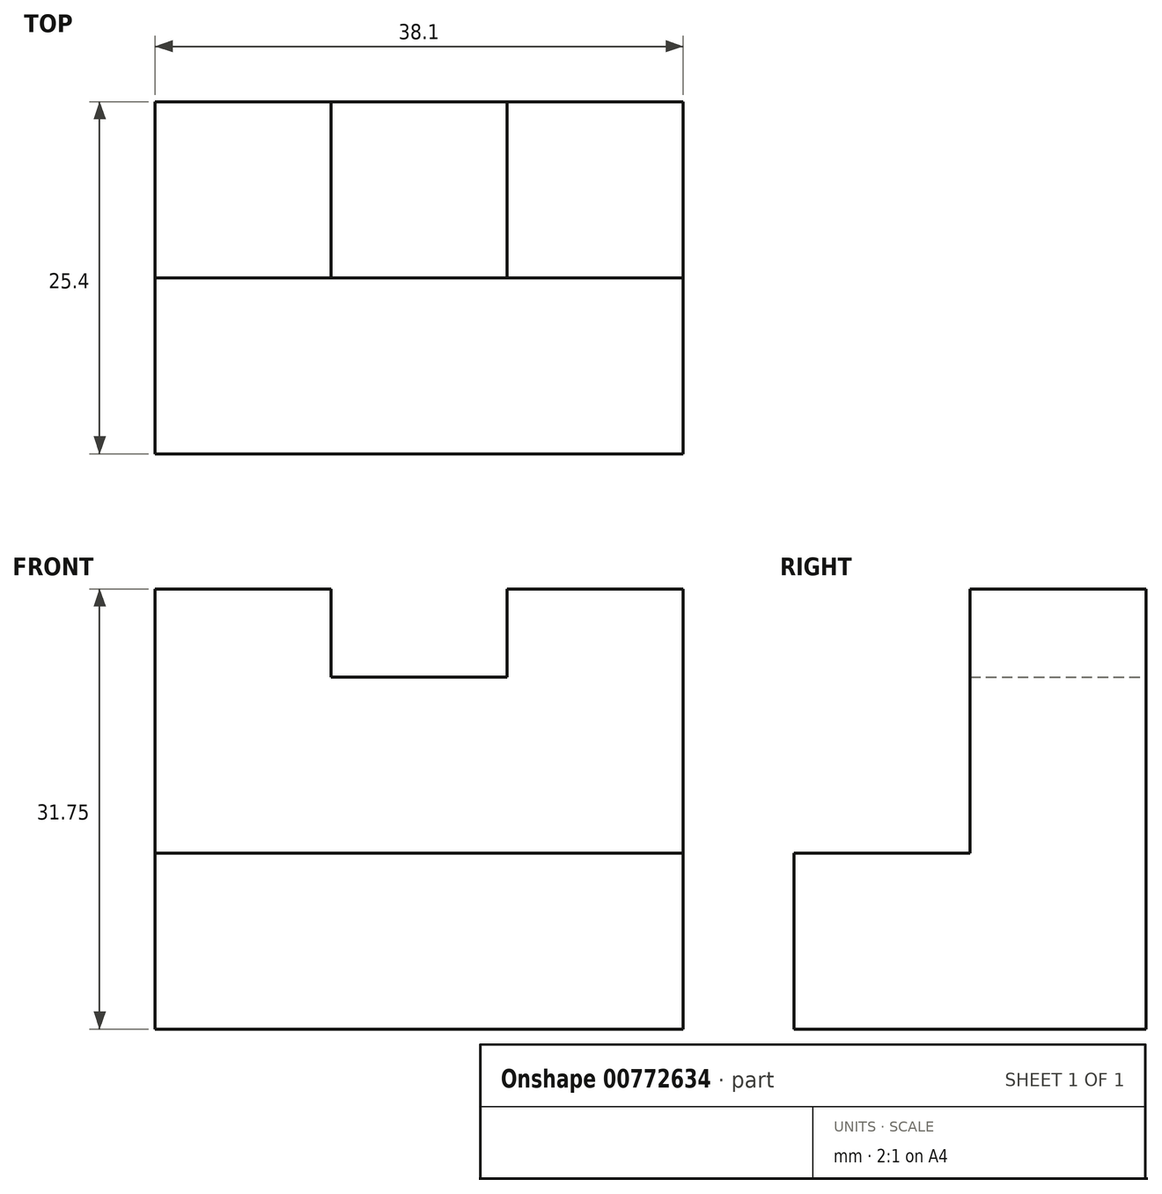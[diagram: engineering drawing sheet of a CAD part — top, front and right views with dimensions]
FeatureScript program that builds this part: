
annotation { "Feature Type Name" : "Feature", "Feature Type Description" : "" }
export const myFeature = defineFeature(function(context is Context, id is Id, definition is map)
    precondition{}
    {
        {
            var Q0;
            Q0=qCreatedBy(makeId("Front.planeOp"),FACE);
            var sketch = newSketch(context, id + "F0", { "sketchPlane" : qUnion([Q0])});
            skLineSegment(sketch, "E0", {"start": v(0, 0) * mm, "end": v(38.1, 0) * mm});
            skLineSegment(sketch, "E1", {"start": v(38.1, 0) * mm, "end": v(38.1, 31.75) * mm});
            skLineSegment(sketch, "E2", {"start": v(38.1, 31.75) * mm, "end": v(0, 31.75) * mm});
            skLineSegment(sketch, "E3", {"start": v(0, 31.75) * mm, "end": v(0, 0) * mm});
            skSolve(sketch);
        }
        {
            var Q0;
            Q0 = qSketchRegion(id + "F0", true);
            extrude(context, id + "F1", {"entities" : qUnion([Q0]), "depth" : 25.4 * mm, "offsetDistance" : 25.4 * mm});
        }
        {
            var Q0;
            Q0=makeQuery(id+"F1.opExtrude","SWEPT_FACE",FACE,{"disambiguationData":[OSD([sQuery(id+"F0.wireOp",EDGE,"E1")])]});
            var sketch = newSketch(context, id + "F2", { "sketchPlane" : qUnion([Q0])});
            skLineSegment(sketch, "E4", {"start": v(-25.4, 0) * mm, "end": v(-25.4, 12.7) * mm});
            skLineSegment(sketch, "E5", {"start": v(-25.4, 12.7) * mm, "end": v(-12.7, 12.7) * mm});
            skLineSegment(sketch, "E6", {"start": v(-12.7, 12.7) * mm, "end": v(-12.7, 31.75) * mm});
            skSolve(sketch);
        }
        {
            var Q0;
            {var subQ0=sQuery(id+"F2.wireOp",EDGE,"E5");Q0=makeQuery(id+"F2.imprint","IMPRINT",FACE,{"disambiguationData":[TD([[makeQuery(id+"F2.imprint","IMPRINT",EDGE,{"derivedFrom":subQ0}),1.0]])]});}
            extrude(context, id + "F3", {"entities" : qUnion([Q0]), "operationType" : NewBodyOperationType.REMOVE, "oppositeDirection" : true, "depth" : 38.1 * mm, "offsetDistance" : 25.4 * mm});
        }
        {
            var Q0;
            Q0=makeQuery(id+"F1.opExtrude","SWEPT_FACE",FACE,{"disambiguationData":[OSD([sQuery(id+"F0.wireOp",EDGE,"E2")])]});
            var sketch = newSketch(context, id + "F4", { "sketchPlane" : qUnion([Q0])});
            skLineSegment(sketch, "E7", {"start": v(38.1, -12.7) * mm, "end": v(25.4, -12.7) * mm});
            skLineSegment(sketch, "E8", {"start": v(25.4, -12.7) * mm, "end": v(25.4, 0) * mm});
            skLineSegment(sketch, "E9", {"start": v(25.4, 0) * mm, "end": v(38.1, 0) * mm});
            skLineSegment(sketch, "E10", {"start": v(38.1, 0) * mm, "end": v(38.1, -12.7) * mm});
            skLineSegment(sketch, "E11", {"start": v(25.4, -12.7) * mm, "end": v(12.7, -12.7) * mm});
            skLineSegment(sketch, "E12", {"start": v(12.7, -12.7) * mm, "end": v(12.7, 0) * mm});
            skLineSegment(sketch, "E13", {"start": v(12.7, 0) * mm, "end": v(25.4, 0) * mm});
            skLineSegment(sketch, "E14", {"start": v(12.7, 0) * mm, "end": v(0, 0) * mm});
            skLineSegment(sketch, "E15", {"start": v(0, 0) * mm, "end": v(0, -12.7) * mm});
            skLineSegment(sketch, "E16", {"start": v(0, -12.7) * mm, "end": v(12.7, -12.7) * mm});
            skSolve(sketch);
        }
        {
            var Q0;
            Q0=makeQuery(id+"F4.imprint","IMPRINT",FACE,{"disambiguationData":[TD([[makeQuery(id+"F4.imprint","IMPRINT",EDGE,{"derivedFrom":sQuery(id+"F4.wireOp",EDGE,"E8")}),1.0]])]});
            extrude(context, id + "F5", {"entities" : qUnion([Q0]), "operationType" : NewBodyOperationType.REMOVE, "oppositeDirection" : true, "depth" : 6.35 * mm, "offsetDistance" : 25.4 * mm});
        }
    });
